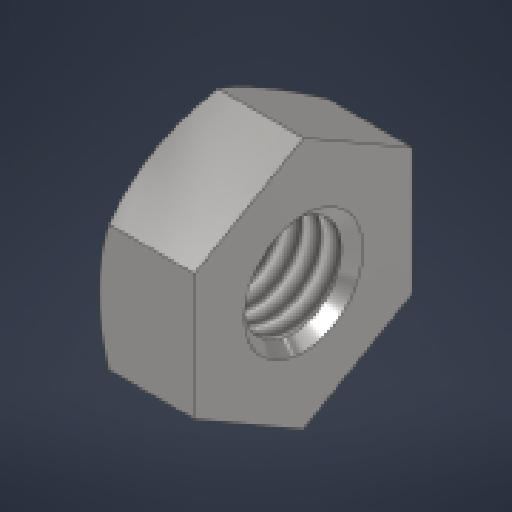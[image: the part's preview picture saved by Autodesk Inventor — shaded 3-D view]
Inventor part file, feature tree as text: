
AUTODESK INVENTOR PART (.ipt)
format: ipt  version: 2024 (Build 280153000, 153)  size: 177,152 bytes
history: native  units: mm
features: other x14, sketch x3, revolve x2, thread x1, extrude x1
ambient origin geometry x8: Origin, YZ Plane, XZ Plane, XY Plane, X Axis, Y Axis, Z Axis, Center Point
bodies: Solid1 (feature_tree)
feature tree (21):
  revolve  "Revolution1"  Angle=360.0deg
  revolve  "Revolution2"  [1 undecoded]
  thread  "Thread1"  [1 undecoded]
  extrude  "Extrusion1"  [1 undecoded]
  other  "cp_XY"
  other  "cp_YZ"
  other  "cp_ZX"
  other  "cp_X"
  other  "cp_Y"
  other  "cp_Z"
  other  "cp_Center"
  other  "nut_to_screw_XY"
  other  "nut_to_screw_YZ"
  other  "nut_to_screw_ZX"
  other  "nut_to_screw_X"
  other  "nut_to_screw_Y"
  other  "nut_to_screw_Z"
  other  "nut_to_screw_Center"
  sketch  "Sketch_1"  dims[d0=360.0deg d1=360.0deg]
  sketch  "Sketch_2"  dims[d2=1.859mm d3=0.0mm d4=2.4mm d5=0.0mm d6=0.0mm]
  sketch  "Sketch_3"
note: 3 required parameter values undecoded (feature->parameter linkage not recoverable at this tier; creation-order binding heuristic only, values carry confidence <= 0.55)